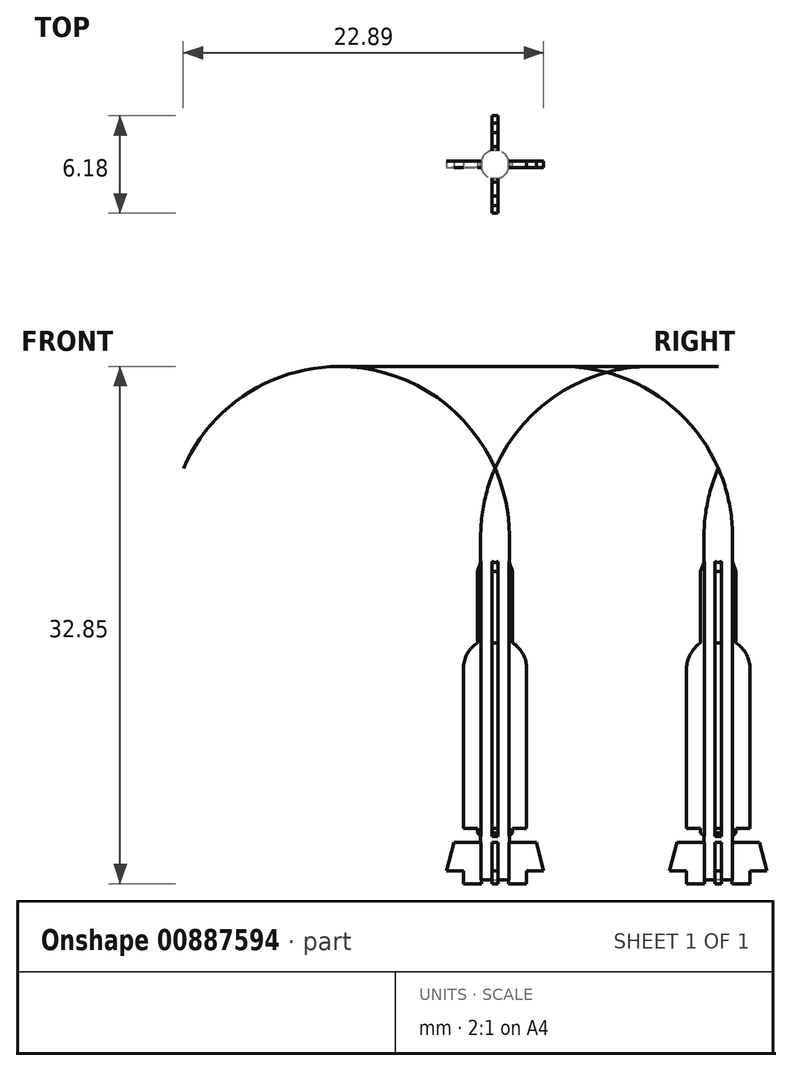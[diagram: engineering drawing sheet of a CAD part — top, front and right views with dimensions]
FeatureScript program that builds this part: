
annotation { "Feature Type Name" : "Feature", "Feature Type Description" : "" }
export const myFeature = defineFeature(function(context is Context, id is Id, definition is map)
    precondition{}
    {
        {
            var Q0;
            Q0=qCreatedBy(makeId("Front.planeOp"),FACE);
            var sketch = newSketch(context, id + "F0", { "sketchPlane" : qUnion([Q0])});
            skLineSegment(sketch, "E0", {"start": v(0, 0) * mm, "end": v(0, 26.15) * mm});
            skLineSegment(sketch, "E1", {"start": v(0.9, 21.8) * mm, "end": v(0.9, 0) * mm});
            skLineSegment(sketch, "E2", {"start": v(0.9, 0) * mm, "end": v(0, 0) * mm});
            skArc(sketch, "E3", {"start": v(0.9, 21.8) * mm, "mid": v(0.68, 24.02) * mm, "end": v(0, 26.15) * mm});
            skSolve(sketch);
        }
        {
            var Q0;
            {var subQ0=sQuery(id+"F0.wireOp",EDGE,"mrwio9nY-PsAZ-Zbfy-NhIU-sYq0QVbgGXAG");Q0=makeQuery(id+"F0.imprint","IMPRINT",FACE,{"disambiguationData":[TD([[makeQuery(id+"F0.imprint","IMPRINT",EDGE,{"derivedFrom":subQ0}),-1.0]])]});}
            var Q1;
            Q1=makeQuery(id+"F0.imprint","IMPRINT",FACE,{"disambiguationData":[TD([[makeQuery(id+"F0.imprint","IMPRINT",EDGE,{"derivedFrom":sQuery(id+"F0.wireOp",EDGE,"rEedh4zr-IGRr-Hqzj-sDLB-QnI7VE1V64O6.bottom")}),-1.0]])]});
            var Q2;
            Q2=makeQuery(id+"F0.imprint","IMPRINT",FACE,{"disambiguationData":[TD([[makeQuery(id+"F0.imprint","IMPRINT",EDGE,{"derivedFrom":sQuery(id+"F0.wireOp",EDGE,"E0")}),-1.0]])]});
            var Q3;
            Q3=makeQuery(id+"F0.imprint","IMPRINT",FACE,{"disambiguationData":[TD([[makeQuery(id+"F0.imprint","IMPRINT",EDGE,{"derivedFrom":sQuery(id+"F0.wireOp",EDGE,"p5wuz8j9-3HT4-kWwn-DjtP-lJmqTNSXSBJY.bottom")}),-1.0]])]});
            var Q4;
            Q4=sQuery(id+"F0.wireOp",EDGE,"E0");
            revolve(context, id + "F1", {"surfaceOperationType" : NewSurfaceOperationType.NEW, "entities" : qUnion([Q0, Q1, Q2, Q3]), "axis" : qUnion([Q4]), "revolveType" : RevolveType.FULL});
        }
        {
            var Q0;
            Q0=qCreatedBy(makeId("Front.planeOp"),FACE);
            var sketch = newSketch(context, id + "F2", { "sketchPlane" : qUnion([Q0])});
            skLineSegment(sketch, "E4", {"start": v(0, 0) * mm, "end": v(0, 22.67) * mm});
            skLineSegment(sketch, "E5", {"start": v(1.12, 2.99) * mm, "end": v(0.8, 2.67) * mm});
            skLineSegment(sketch, "E6", {"start": v(0.8, 2.4) * mm, "end": v(2.62, 2.4) * mm});
            skLineSegment(sketch, "E7", {"start": v(0.9, 0) * mm, "end": v(0.9, 32.87) * mm, "construction": true});
            skPoint(sketch, "E8", {"position": v(0.9, 2.78) * mm});
            skLineSegment(sketch, "E9", {"start": v(2.01, -0.24) * mm, "end": v(0.87, -0.24) * mm});
            skLineSegment(sketch, "E10", {"start": v(1.12, 2.99) * mm, "end": v(1.12, 3.26) * mm});
            skLineSegment(sketch, "E11", {"start": v(2.01, -0.24) * mm, "end": v(2.01, 0.6) * mm});
            skLineSegment(sketch, "E12", {"start": v(2.01, 0.6) * mm, "end": v(3.1, 0.6) * mm});
            skLineSegment(sketch, "E13", {"start": v(3.1, 0.6) * mm, "end": v(2.62, 2.4) * mm});
            skLineSegment(sketch, "E14", {"start": v(0.8, 2.67) * mm, "end": v(0.8, 2.4) * mm});
            skLineSegment(sketch, "E15", {"start": v(1.12, 3.26) * mm, "end": v(2.01, 3.26) * mm});
            skLineSegment(sketch, "E16", {"start": v(2.01, 3.26) * mm, "end": v(2.01, 13.4) * mm});
            skArc(sketch, "E17", {"start": v(2.01, 13.4) * mm, "mid": v(1.72, 14.45) * mm, "end": v(0.9, 15.2) * mm});
            skPoint(sketch, "E18", {"position": v(0.9, 15.2) * mm});
            skLineSegment(sketch, "E19", {"start": v(1.12, 15.07) * mm, "end": v(1.12, 19.6) * mm});
            skLineSegment(sketch, "E20", {"start": v(1.12, 19.6) * mm, "end": v(0, 22.67) * mm});
            skPoint(sketch, "E21", {"position": v(0.9, 20.17) * mm});
            skLineSegment(sketch, "E22.0", {"start": v(0.9, 0) * mm, "end": v(-0.9, 0) * mm});
            skLineSegment(sketch, "E23", {"start": v(0.87, -0.24) * mm, "end": v(0.87, 1.63) * mm});
            skLineSegment(sketch, "E24", {"start": v(0.87, 1.63) * mm, "end": v(0, 1.63) * mm});
            skSolve(sketch);
        }
        {
            var Q0;
            Q0=qSketchRegion(id+"F2",true);
            extrude(context, id + "F3", {"entities" : qUnion([Q0]), "operationType" : NewBodyOperationType.ADD, "depth" : .4 * mm, "offsetDistance" : 25 * mm, "symmetric" : true});
        }
        {
            var Q0;
            Q0=makeQuery(id+"F1.opRevolve","SWEPT_BODY",BODY,{"disambiguationData":[OSD([sQuery(id+"F0.wireOp",EDGE,"E0"),sQuery(id+"F0.wireOp",EDGE,"E1"),sQuery(id+"F0.wireOp",EDGE,"E2"),sQuery(id+"F0.wireOp",EDGE,"2EiOItwe-9FNA-eY8p-DkXH-AMy5AHyUmzZA"),sQuery(id+"F0.wireOp",EDGE,"E3")])]});
            var Q1;
            Q1=makeQuery(id+"F1.opRevolve","SWEPT_FACE",FACE,{"disambiguationData":[OSD([sQuery(id+"F0.wireOp",EDGE,"E1")])]});
            circularPattern(context, id + "F4", {"operationType" : NewBodyOperationType.ADD, "entities" : qUnion([Q0]), "axis" : qUnion([Q1]), "angle" : 360 * degree, "instanceCount" : 4, "equalSpace" : true, "computeTransformsWithoutBuiltin" : true});
        }
    });
